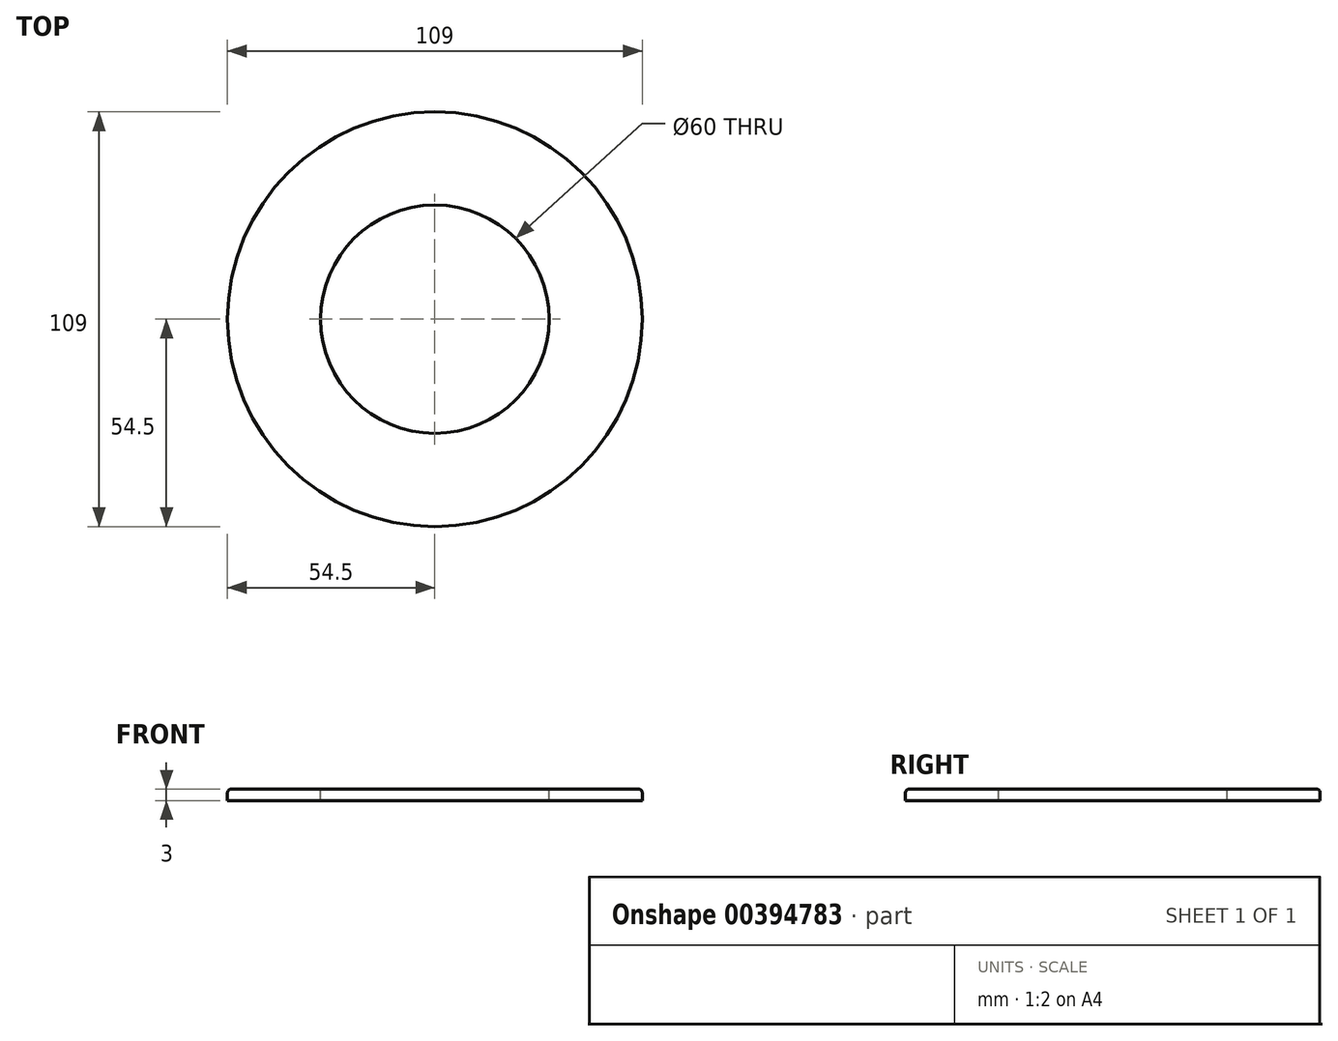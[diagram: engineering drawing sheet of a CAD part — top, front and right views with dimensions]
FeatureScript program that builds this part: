
annotation { "Feature Type Name" : "Feature", "Feature Type Description" : "" }
export const myFeature = defineFeature(function(context is Context, id is Id, definition is map)
    precondition{}
    {
        {
            var Q0;
            Q0=qCreatedBy(makeId("Top.planeOp"),FACE);
            var sketch = newSketch(context, id + "F0", { "sketchPlane" : qUnion([Q0])});
            skCircle(sketch, "E0.0", {"center": v(0, 0) * mm, "radius": 54.5 * mm});
            skCircle(sketch, "E1", {"center": v(0, 0) * mm, "radius": 30 * mm});
            skSolve(sketch);
        }
        {
            var Q0;
            Q0=makeQuery(id+"F0.imprint","IMPRINT",FACE,{"disambiguationData":[TD([[makeQuery(id+"F0.imprint","IMPRINT",EDGE,{"derivedFrom":sQuery(id+"F0.wireOp",EDGE,"E0.0")}),1.0]])]});
            extrude(context, id + "F1", {"entities" : qUnion([Q0]), "oppositeDirection" : true, "depth" : 3 * mm});
        }
        {
            var Q0;
            Q0=makeQuery(id+"F1.opExtrude","CAP_EDGE",EDGE,{"disambiguationData":[OSD([sQuery(id+"F0.wireOp",EDGE,"E0.0")])],"isStart":true});
            fillet(context, id + "F2", {"entities" : qUnion([Q0]), "radius" : 1 * mm, "tangentPropagation" : true, "allowEdgeOverflow" : false});
        }
    });
